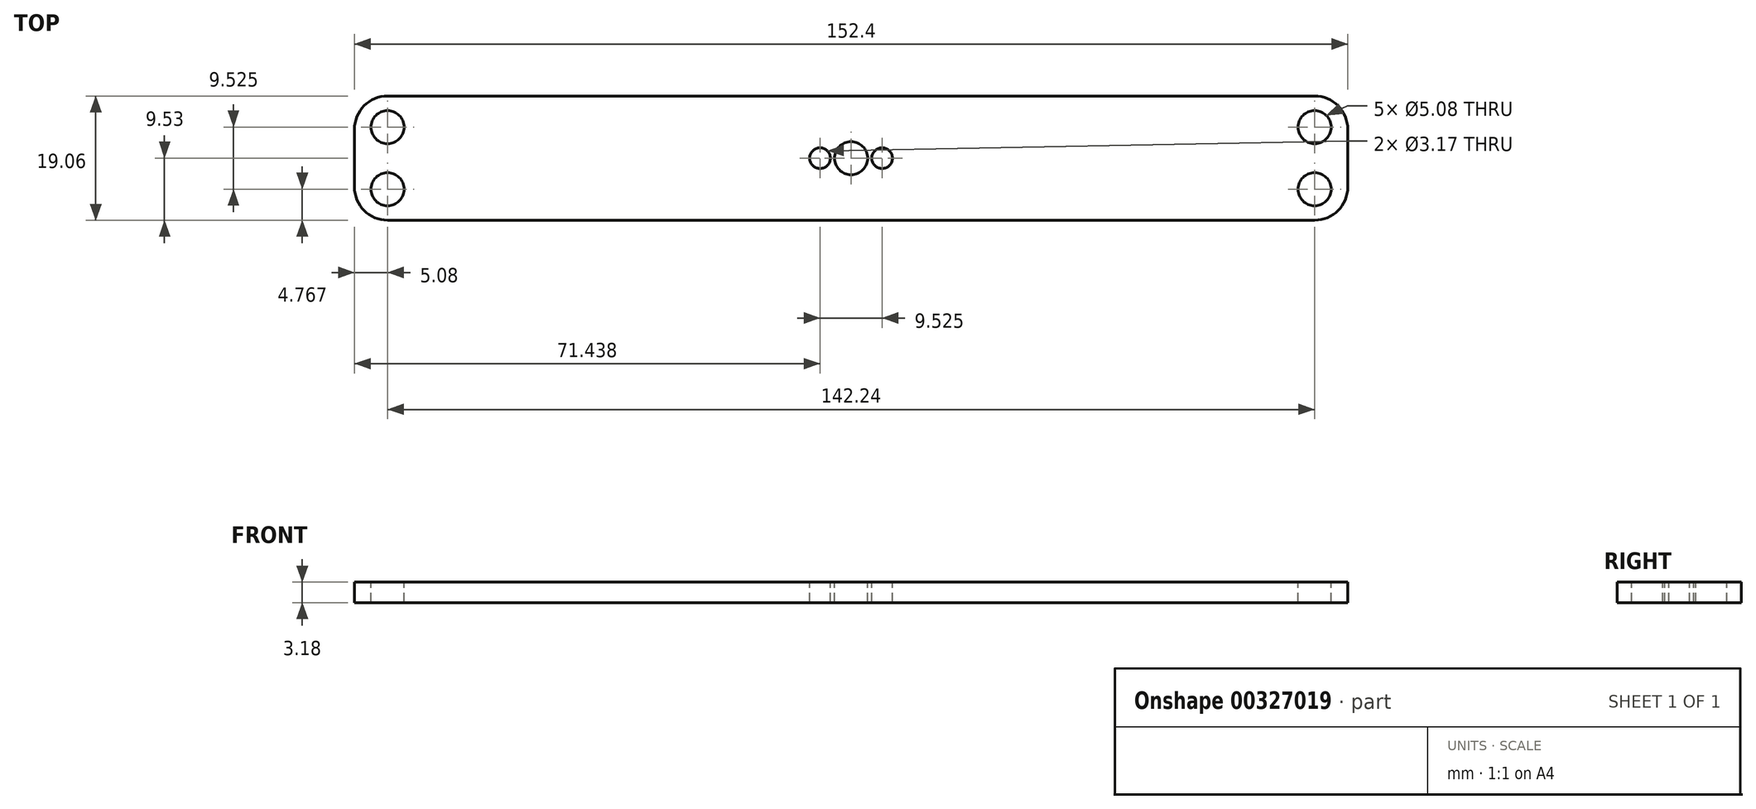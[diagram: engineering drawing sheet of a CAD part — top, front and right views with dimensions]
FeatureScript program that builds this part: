
annotation { "Feature Type Name" : "Feature", "Feature Type Description" : "" }
export const myFeature = defineFeature(function(context is Context, id is Id, definition is map)
    precondition{}
    {
        {
            var Q0;
            Q0=qCreatedBy(makeId("Top.planeOp"),FACE);
            var sketch = newSketch(context, id + "F0", { "sketchPlane" : qUnion([Q0])});
            skLineSegment(sketch, "E0.bottom", {"start": v(-76.2, 9.52) * mm, "end": v(76.2, 9.52) * mm});
            skLineSegment(sketch, "E0.top", {"start": v(-76.2, -9.53) * mm, "end": v(76.2, -9.53) * mm});
            skLineSegment(sketch, "E0.left", {"start": v(-76.2, 9.52) * mm, "end": v(-76.2, -9.53) * mm});
            skLineSegment(sketch, "E0.right", {"start": v(76.2, 9.53) * mm, "end": v(76.2, -9.52) * mm});
            skSolve(sketch);
        }
        {
            var Q0;
            Q0=makeQuery(id+"F0.imprint","IMPRINT",FACE,{"disambiguationData":[TD([[makeQuery(id+"F0.imprint","IMPRINT",EDGE,{"derivedFrom":sQuery(id+"F0.wireOp",EDGE,"E0.bottom")}),-1.0]])]});
            extrude(context, id + "F1", {"entities" : qUnion([Q0]), "depth" : 3.17 * mm});
        }
        {
            var Q0;
            Q0=makeQuery(id+"F1.opExtrude","CAP_FACE",FACE,{"disambiguationData":[OSD([sQuery(id+"F0.wireOp",EDGE,"E0.bottom"),sQuery(id+"F0.wireOp",EDGE,"E0.top"),sQuery(id+"F0.wireOp",EDGE,"E0.left"),sQuery(id+"F0.wireOp",EDGE,"E0.right")])],"isStart":false});
            var sketch = newSketch(context, id + "F2", { "sketchPlane" : qUnion([Q0])});
            skCircle(sketch, "E1", {"center": v(-71.12, 4.76) * mm, "radius": 2.54 * mm});
            skCircle(sketch, "E2", {"center": v(-71.12, -4.76) * mm, "radius": 2.54 * mm});
            skCircle(sketch, "E3.MirrorC", {"center": v(71.12, 4.76) * mm, "radius": 2.54 * mm});
            skCircle(sketch, "E4.MirrorC", {"center": v(71.12, -4.76) * mm, "radius": 2.54 * mm});
            skSolve(sketch);
        }
        {
            var Q0;
            Q0 = qSketchRegion(id + "F2", true);
            extrude(context, id + "F3", {"entities" : qUnion([Q0]), "operationType" : NewBodyOperationType.REMOVE, "endBound" : BoundingType.THROUGH_ALL, "oppositeDirection" : true, "depth" : 25.4 * mm});
        }
        {
            var Q0;
            Q0=makeQuery(id+"F1.opExtrude","SWEPT_EDGE",EDGE,{"disambiguationData":[OSD([sQuery(id+"F0.wireOp",EDGE,"E0.bottom"),sQuery(id+"F0.wireOp",EDGE,"E0.left")])]});
            var Q1;
            Q1=makeQuery(id+"F1.opExtrude","SWEPT_EDGE",EDGE,{"disambiguationData":[OSD([sQuery(id+"F0.wireOp",EDGE,"E0.top"),sQuery(id+"F0.wireOp",EDGE,"E0.left")])]});
            var Q2;
            Q2=makeQuery(id+"F1.opExtrude","SWEPT_EDGE",EDGE,{"disambiguationData":[OSD([sQuery(id+"F0.wireOp",EDGE,"E0.bottom"),sQuery(id+"F0.wireOp",EDGE,"E0.right")])]});
            var Q3;
            Q3=makeQuery(id+"F1.opExtrude","SWEPT_EDGE",EDGE,{"disambiguationData":[OSD([sQuery(id+"F0.wireOp",EDGE,"E0.top"),sQuery(id+"F0.wireOp",EDGE,"E0.right")])]});
            fillet(context, id + "F4", {"entities" : qUnion([Q0, Q1, Q2, Q3]), "radius" : 5.08 * mm, "tangentPropagation" : true, "allowEdgeOverflow" : false});
        }
        {
            var Q0;
            Q0=makeQuery(id+"F1.opExtrude","CAP_FACE",FACE,{"disambiguationData":[OSD([sQuery(id+"F0.wireOp",EDGE,"E0.bottom"),sQuery(id+"F0.wireOp",EDGE,"E0.top"),sQuery(id+"F0.wireOp",EDGE,"E0.left"),sQuery(id+"F0.wireOp",EDGE,"E0.right")])],"isStart":false});
            var sketch = newSketch(context, id + "F5", { "sketchPlane" : qUnion([Q0])});
            skCircle(sketch, "E5", {"center": v(0, 0) * mm, "radius": 2.54 * mm});
            skCircle(sketch, "E6", {"center": v(-4.76, 0) * mm, "radius": 1.59 * mm});
            skCircle(sketch, "E7", {"center": v(4.76, 0) * mm, "radius": 1.59 * mm});
            skSolve(sketch);
        }
        {
            var Q0;
            Q0=makeQuery(id+"F5.imprint","IMPRINT",FACE,{"disambiguationData":[TD([[makeQuery(id+"F5.imprint","IMPRINT",EDGE,{"derivedFrom":sQuery(id+"F5.wireOp",EDGE,"E5")}),1.0]])]});
            var Q1;
            Q1=makeQuery(id+"F5.imprint","IMPRINT",FACE,{"disambiguationData":[TD([[makeQuery(id+"F5.imprint","IMPRINT",EDGE,{"derivedFrom":sQuery(id+"F5.wireOp",EDGE,"E6")}),1.0]])]});
            var Q2;
            Q2=makeQuery(id+"F5.imprint","IMPRINT",FACE,{"disambiguationData":[TD([[makeQuery(id+"F5.imprint","IMPRINT",EDGE,{"derivedFrom":sQuery(id+"F5.wireOp",EDGE,"E7")}),1.0]])]});
            extrude(context, id + "F6", {"entities" : qUnion([Q0, Q1, Q2]), "operationType" : NewBodyOperationType.REMOVE, "endBound" : BoundingType.THROUGH_ALL, "oppositeDirection" : true, "depth" : 25.4 * mm});
        }
    });
